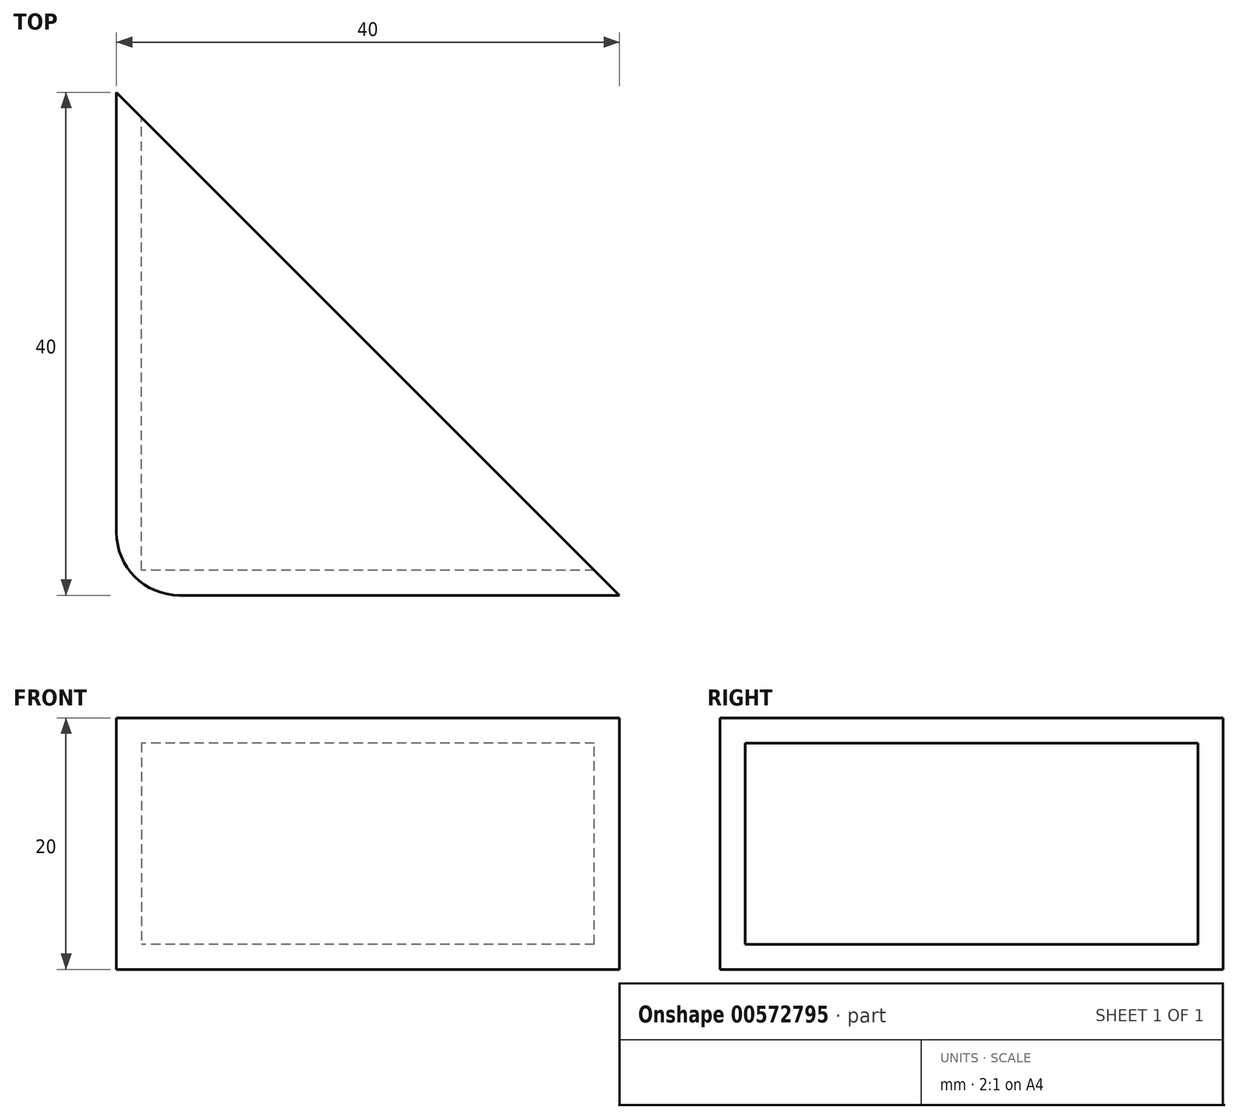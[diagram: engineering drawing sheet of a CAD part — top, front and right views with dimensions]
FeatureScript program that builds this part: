
annotation { "Feature Type Name" : "Feature", "Feature Type Description" : "" }
export const myFeature = defineFeature(function(context is Context, id is Id, definition is map)
    precondition{}
    {
        {
            var Q0;
            Q0=qCreatedBy(makeId("Top.planeOp"),FACE);
            var sketch = newSketch(context, id + "F0", { "sketchPlane" : qUnion([Q0])});
            skLineSegment(sketch, "E0.bottom", {"start": v(20, -20) * mm, "end": v(-20, -20) * mm});
            skLineSegment(sketch, "E0.top", {"start": v(20, 20) * mm, "end": v(-20, 20) * mm});
            skLineSegment(sketch, "E0.left", {"start": v(20, -20) * mm, "end": v(20, 20) * mm});
            skLineSegment(sketch, "E0.right", {"start": v(-20, -20) * mm, "end": v(-20, 20) * mm});
            skPoint(sketch, "E0.middle", {"position": v(0, 0) * mm});
            skSolve(sketch);
        }
        {
            var Q0;
            Q0=makeQuery(id+"F0.imprint","IMPRINT",FACE,{"disambiguationData":[TD([[makeQuery(id+"F0.imprint","IMPRINT",EDGE,{"derivedFrom":sQuery(id+"F0.wireOp",EDGE,"E0.bottom")}),-1.0]])]});
            extrude(context, id + "F1", {"entities" : qUnion([Q0]), "depth" : 20 * mm, "offsetDistance" : 25 * mm});
        }
        {
            var Q0;
            Q0=makeQuery(id+"F1.opExtrude","SWEPT_FACE",FACE,{"disambiguationData":[OSD([sQuery(id+"F0.wireOp",EDGE,"E0.left")])]});
            var Q1;
            Q1=makeQuery(id+"F1.opExtrude","SWEPT_FACE",FACE,{"disambiguationData":[OSD([sQuery(id+"F0.wireOp",EDGE,"E0.top")])]});
            shell(context, id + "F2", {"entities" : qUnion([Q0, Q1]), "thickness" : 2 * mm});
        }
        {
            var Q0;
            Q0=makeQuery(id+"F1.opExtrude","SWEPT_EDGE",EDGE,{"disambiguationData":[OSD([sQuery(id+"F0.wireOp",EDGE,"E0.top"),sQuery(id+"F0.wireOp",EDGE,"E0.left")])]});
            var Q1;
            Q1=makeQuery(id+"F2.opShell","OFFSET_EDGE",EDGE,{"disambiguationData":[OSD([sQuery(id+"F0.wireOp",EDGE,"E0.top"),sQuery(id+"F0.wireOp",EDGE,"E0.left")])]});
            chamfer(context, id + "F3", {"entities" : qUnion([Q0, Q1]), "width" : 40 * mm, "tangentPropagation" : true});
        }
        {
            var Q0;
            Q0=makeQuery(id+"F1.opExtrude","SWEPT_EDGE",EDGE,{"disambiguationData":[OSD([sQuery(id+"F0.wireOp",EDGE,"E0.bottom"),sQuery(id+"F0.wireOp",EDGE,"E0.right")])]});
            fillet(context, id + "F4", {"entities" : qUnion([Q0]), "radius" : 5 * mm, "tangentPropagation" : true, "allowEdgeOverflow" : false});
        }
    });
